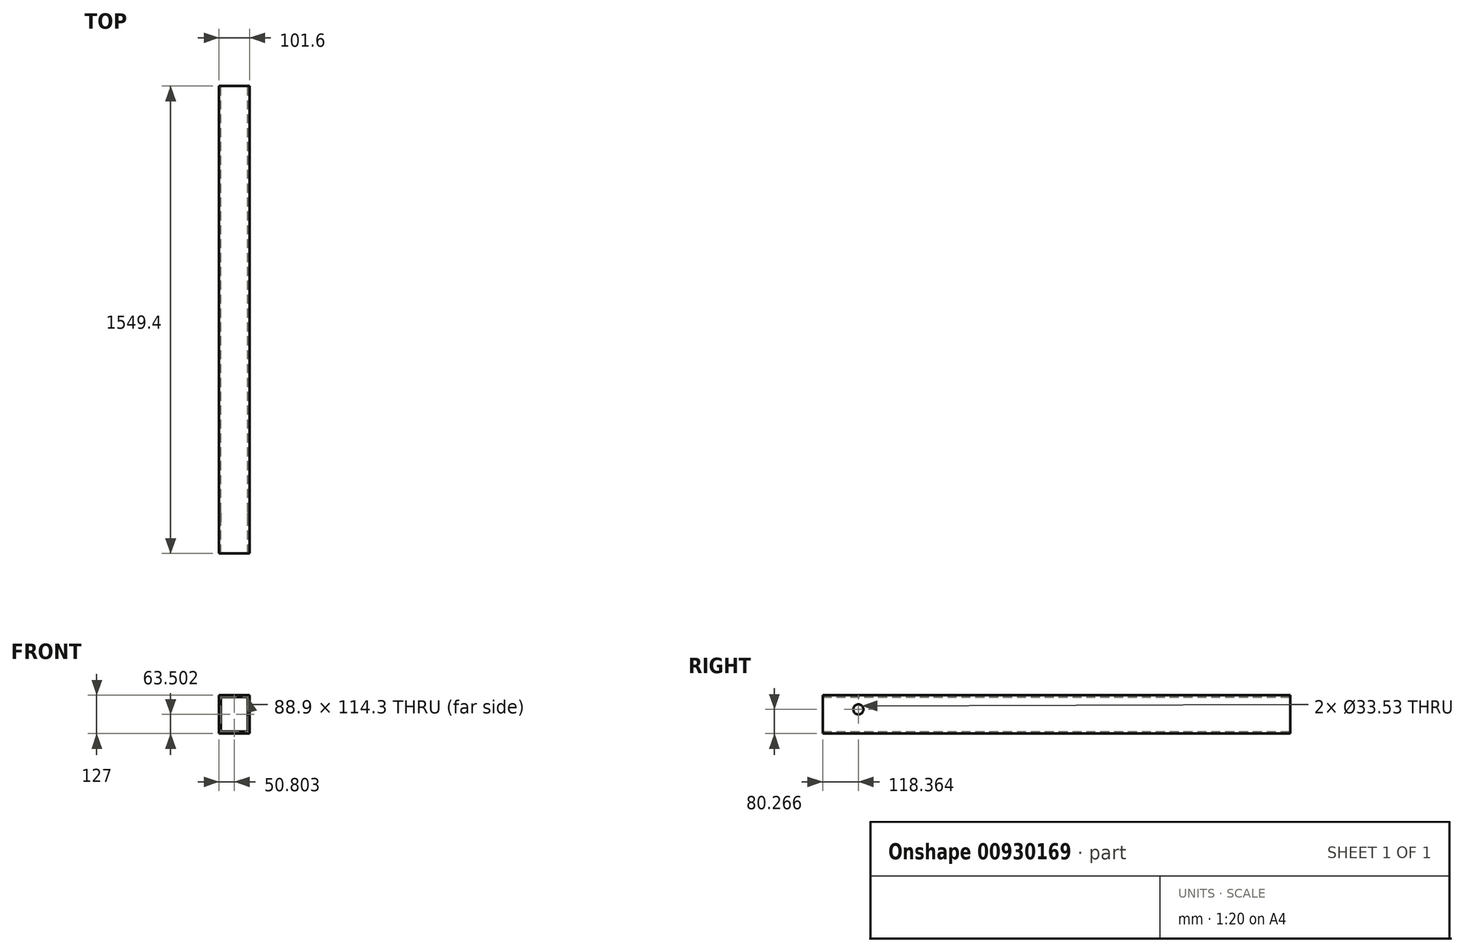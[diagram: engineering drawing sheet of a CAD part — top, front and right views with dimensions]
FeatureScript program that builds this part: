
annotation { "Feature Type Name" : "Feature", "Feature Type Description" : "" }
export const myFeature = defineFeature(function(context is Context, id is Id, definition is map)
    precondition{}
    {
        {
            var Q0;
            Q0=qCreatedBy(makeId("Front.planeOp"),FACE);
            var sketch = newSketch(context, id + "F0", { "sketchPlane" : qUnion([Q0])});
            skLineSegment(sketch, "E0.bottom", {"start": v(-65, 68.6) * mm, "end": v(36.6, 68.6) * mm});
            skLineSegment(sketch, "E0.top", {"start": v(-65, -58.4) * mm, "end": v(36.6, -58.4) * mm});
            skLineSegment(sketch, "E0.left", {"start": v(-65, 68.6) * mm, "end": v(-65, -58.4) * mm});
            skLineSegment(sketch, "E0.right", {"start": v(36.6, 68.6) * mm, "end": v(36.6, -58.4) * mm});
            skLineSegment(sketch, "E1.bottom", {"start": v(-58.66, 62.24) * mm, "end": v(30.24, 62.24) * mm});
            skLineSegment(sketch, "E1.top", {"start": v(-58.66, -52.06) * mm, "end": v(30.24, -52.06) * mm});
            skLineSegment(sketch, "E1.left", {"start": v(-58.66, 62.24) * mm, "end": v(-58.66, -52.06) * mm});
            skLineSegment(sketch, "E1.right", {"start": v(30.24, 62.24) * mm, "end": v(30.24, -52.06) * mm});
            skSolve(sketch);
        }
        {
            var Q0;
            Q0=makeQuery(id+"F0.imprint","IMPRINT",FACE,{"disambiguationData":[TD([[makeQuery(id+"F0.imprint","IMPRINT",EDGE,{"derivedFrom":sQuery(id+"F0.wireOp",EDGE,"E0.bottom")}),-1.0]])]});
            var Q1;
            Q1 = qSketchRegion(id + "F2", true);
            extrude(context, id + "F1", {"entities" : qUnion([Q0, Q1]), "depth" : 1524 * mm, "offsetDistance" : 25.4 * mm, "hasSecondDirection" : true, "secondDirectionOppositeDirection" : true, "secondDirectionDepth" : 25.4 * mm});
        }
        {
            var Q0;
            Q0=makeQuery(id+"F1.opExtrude","SWEPT_FACE",FACE,{"disambiguationData":[OSD([sQuery(id+"F0.wireOp",EDGE,"E0.right")])]});
            var sketch = newSketch(context, id + "F2", { "sketchPlane" : qUnion([Q0])});
            skCircle(sketch, "E2", {"center": v(-1405.64, 21.86) * mm, "radius": 16.76 * mm});
            skLineSegment(sketch, "E3", {"start": v(-1524, 36.84) * mm, "end": v(-1460.5, 36.84) * mm});
            skLineSegment(sketch, "E4", {"start": v(-1460.5, 36.84) * mm, "end": v(-1460.5, -26.66) * mm});
            skLineSegment(sketch, "E5", {"start": v(-1460.5, -26.66) * mm, "end": v(-1524, -26.66) * mm});
            skSolve(sketch);
        }
        {
            var Q0;
            Q0=makeQuery(id+"F2.imprint","IMPRINT",FACE,{"disambiguationData":[TD([[makeQuery(id+"F2.imprint","IMPRINT",EDGE,{"derivedFrom":sQuery(id+"F2.wireOp",EDGE,"E2")}),1.0]])]});
            extrude(context, id + "F3", {"entities" : qUnion([Q0]), "operationType" : NewBodyOperationType.REMOVE, "oppositeDirection" : true, "depth" : 127 * mm, "offsetDistance" : 25.4 * mm});
        }
    });
